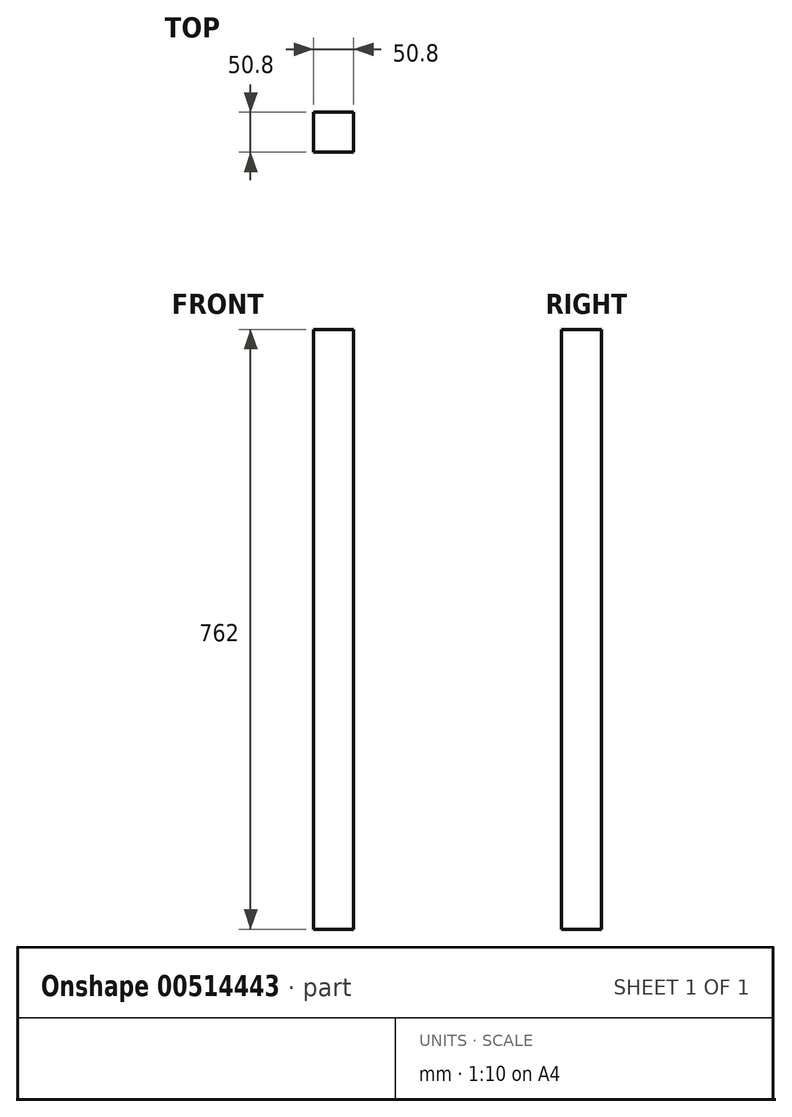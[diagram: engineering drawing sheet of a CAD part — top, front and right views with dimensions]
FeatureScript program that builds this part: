
annotation { "Feature Type Name" : "Feature", "Feature Type Description" : "" }
export const myFeature = defineFeature(function(context is Context, id is Id, definition is map)
    precondition{}
    {
        {
            var Q0;
            Q0=qCreatedBy(makeId("Front.planeOp"),FACE);
            var sketch = newSketch(context, id + "F0", { "sketchPlane" : qUnion([Q0])});
            skLineSegment(sketch, "E0.bottom", {"start": v(0, 0) * mm, "end": v(-25.4, 0) * mm});
            skLineSegment(sketch, "E0.top", {"start": v(0, 762) * mm, "end": v(-25.4, 762) * mm});
            skLineSegment(sketch, "E0.left", {"start": v(0, 0) * mm, "end": v(0, 762) * mm});
            skLineSegment(sketch, "E0.right", {"start": v(-25.4, 0) * mm, "end": v(-25.4, 762) * mm});
            skLineSegment(sketch, "E1", {"start": v(-25.4, 568.66) * mm, "end": v(-25.4, 568.66) * mm});
            skSolve(sketch);
        }
        {
            var Q0;
            {var subQ1=sQuery(id+"F0.wireOp",EDGE,"E0.bottom");Q0=makeQuery(id+"F0.imprint","IMPRINT",FACE,{"disambiguationData":[TD([[makeQuery(id+"F0.imprint","IMPRINT",EDGE,{"derivedFrom":subQ1}),-1.0]])]});}
            extrude(context, id + "F1", {"entities" : qUnion([Q0]), "depth" : 50.8 * mm, "offsetDistance" : 25.4 * mm});
        }
        {
            var Q0;
            Q0=makeQuery(id+"F1.opExtrude","SWEPT_FACE",FACE,{"disambiguationData":[OSD([sQuery(id+"F0.wireOp",EDGE,"E0.left")])]});
            extrude(context, id + "F2", {"entities" : qUnion([Q0]), "operationType" : NewBodyOperationType.ADD, "depth" : 25.4 * mm, "offsetDistance" : 25.4 * mm});
        }
    });
